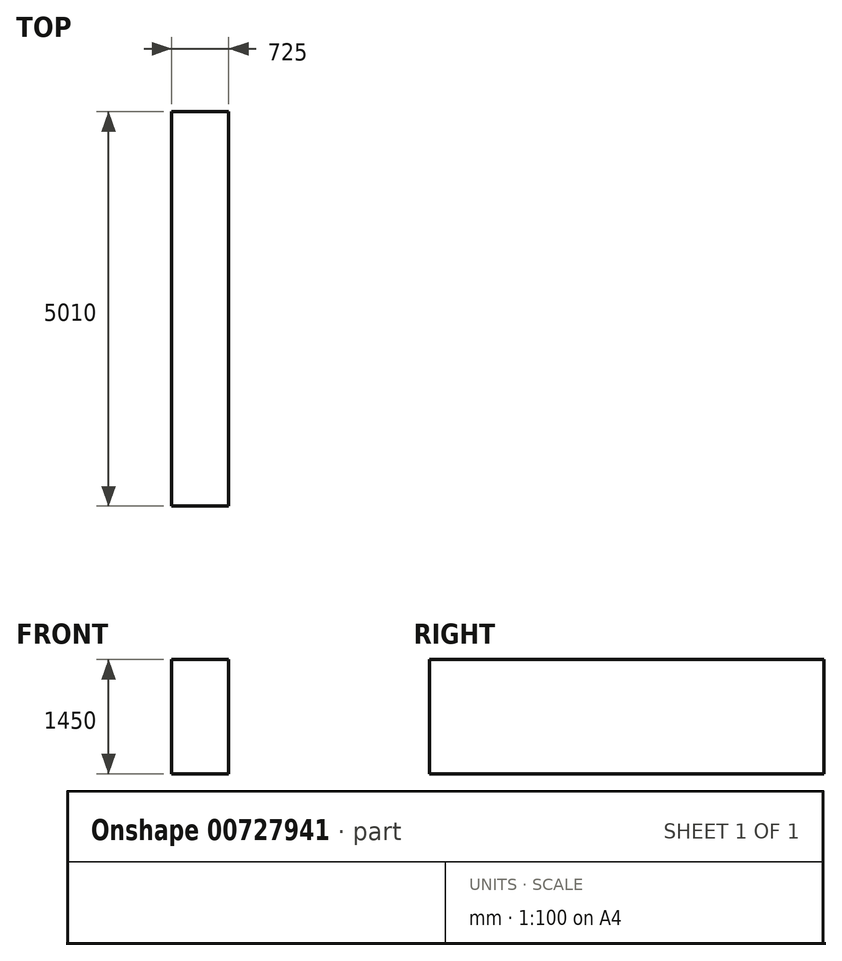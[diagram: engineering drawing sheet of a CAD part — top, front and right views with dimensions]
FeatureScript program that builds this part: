
annotation { "Feature Type Name" : "Feature", "Feature Type Description" : "" }
export const myFeature = defineFeature(function(context is Context, id is Id, definition is map)
    precondition{}
    {
        {
            var Q0;
            Q0=qCreatedBy(makeId("Top.planeOp"),FACE);
            var sketch = newSketch(context, id + "F0", { "sketchPlane" : qUnion([Q0])});
            skLineSegment(sketch, "E0.bottom", {"start": v(362.5, -2505) * mm, "end": v(-362.5, -2505) * mm});
            skLineSegment(sketch, "E0.top", {"start": v(362.5, 2505) * mm, "end": v(-362.5, 2505) * mm});
            skLineSegment(sketch, "E0.left", {"start": v(362.5, -2505) * mm, "end": v(362.5, 2505) * mm});
            skLineSegment(sketch, "E0.right", {"start": v(-362.5, -2505) * mm, "end": v(-362.5, 2505) * mm});
            skPoint(sketch, "E0.middle", {"position": v(0, 0) * mm});
            skSolve(sketch);
        }
        {
            var Q0;
            Q0=makeQuery(id+"F0.imprint","IMPRINT",FACE,{"disambiguationData":[TD([[makeQuery(id+"F0.imprint","IMPRINT",EDGE,{"derivedFrom":sQuery(id+"F0.wireOp",EDGE,"E0.bottom")}),-1.0]])]});
            extrude(context, id + "F1", {"entities" : qUnion([Q0]), "depth" : 1450 * mm, "offsetDistance" : 25.4 * mm});
        }
    });
